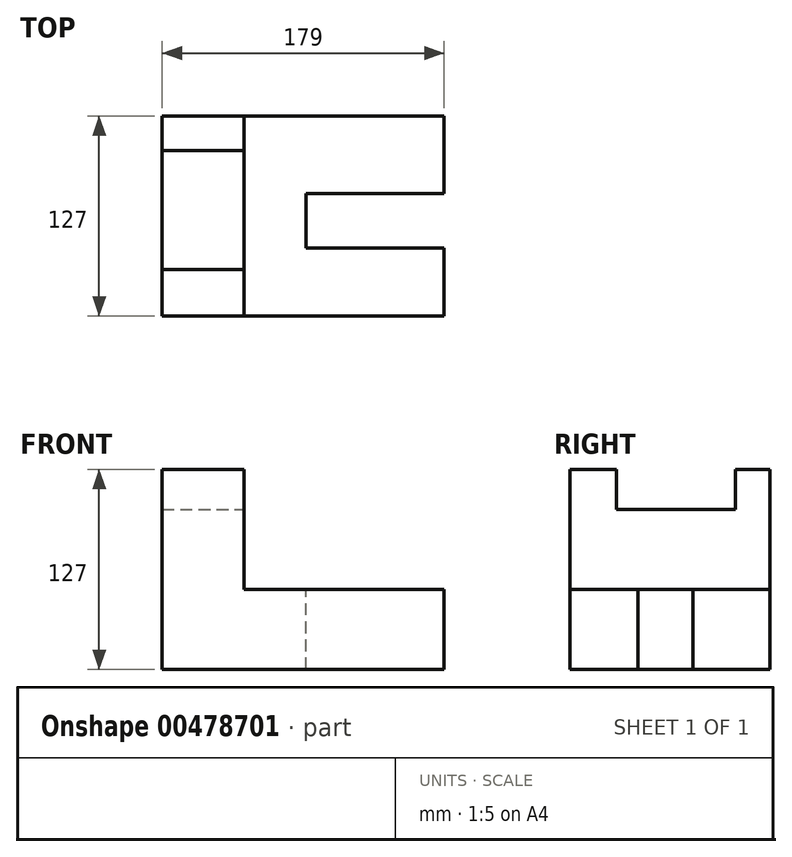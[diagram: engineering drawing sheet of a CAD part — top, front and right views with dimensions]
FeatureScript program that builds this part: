
annotation { "Feature Type Name" : "Feature", "Feature Type Description" : "" }
export const myFeature = defineFeature(function(context is Context, id is Id, definition is map)
    precondition{}
    {
        {
            var Q0;
            Q0=qCreatedBy(makeId("Front.planeOp"),FACE);
            var sketch = newSketch(context, id + "F0", { "sketchPlane" : qUnion([Q0])});
            skLineSegment(sketch, "E0", {"start": v(-127, 76.2) * mm, "end": v(-127, -50.8) * mm});
            skLineSegment(sketch, "E1", {"start": v(-127, -50.8) * mm, "end": v(52, -50.8) * mm});
            skLineSegment(sketch, "E2", {"start": v(52, -50.8) * mm, "end": v(52, 0) * mm});
            skLineSegment(sketch, "E3", {"start": v(52, 0) * mm, "end": v(-75, 0) * mm});
            skLineSegment(sketch, "E4", {"start": v(-75, 0) * mm, "end": v(-75, 76.2) * mm});
            skLineSegment(sketch, "E5", {"start": v(-75, 76.2) * mm, "end": v(-127, 76.2) * mm});
            skSolve(sketch);
        }
        {
            var Q0;
            Q0 = qSketchRegion(id + "F0", true);
            extrude(context, id + "F1", {"entities" : qUnion([Q0]), "depth" : 127 * mm});
        }
        {
            var Q0;
            Q0=makeQuery(id+"F1.opExtrude","SWEPT_FACE",FACE,{"disambiguationData":[OSD([sQuery(id+"F0.wireOp",EDGE,"E5")])]});
            var sketch = newSketch(context, id + "F2", { "sketchPlane" : qUnion([Q0])});
            skLineSegment(sketch, "E6", {"start": v(-127, -97.5) * mm, "end": v(-75, -97.5) * mm});
            skLineSegment(sketch, "E7", {"start": v(-127, -22) * mm, "end": v(-75, -22) * mm});
            skSolve(sketch);
        }
        {
            var Q0;
            {var subQ0=sQuery(id+"F2.wireOp",EDGE,"E6");Q0=makeQuery(id+"F2.imprint","IMPRINT",FACE,{"disambiguationData":[TD([[makeQuery(id+"F2.imprint","IMPRINT",EDGE,{"derivedFrom":subQ0}),1.0]])]});}
            extrude(context, id + "F3", {"entities" : qUnion([Q0]), "operationType" : NewBodyOperationType.REMOVE, "oppositeDirection" : true, "depth" : 25.4 * mm});
        }
        {
            var Q0;
            Q0=makeQuery(id+"F1.opExtrude","SWEPT_FACE",FACE,{"disambiguationData":[OSD([sQuery(id+"F0.wireOp",EDGE,"E3")])]});
            var sketch = newSketch(context, id + "F4", { "sketchPlane" : qUnion([Q0])});
            skLineSegment(sketch, "E8", {"start": v(52, -83.78) * mm, "end": v(-35.83, -83.78) * mm});
            skLineSegment(sketch, "E9", {"start": v(-35.83, -83.78) * mm, "end": v(-35.83, -49.1) * mm});
            skLineSegment(sketch, "E10", {"start": v(-35.83, -49.1) * mm, "end": v(52, -49.1) * mm});
            skPoint(sketch, "E10.endSnap0", {"position": v(52, -63.5) * mm});
            skSolve(sketch);
        }
        {
            var Q0;
            Q0 = qSketchRegion(id + "F4", true);
            var Q1;
            {var subQ0=sQuery(id+"F4.wireOp",EDGE,"E8");Q1=makeQuery(id+"F4.imprint","IMPRINT",FACE,{"disambiguationData":[TD([[makeQuery(id+"F4.imprint","IMPRINT",EDGE,{"derivedFrom":subQ0}),-1.0]])]});}
            extrude(context, id + "F5", {"entities" : qUnion([Q0, Q1]), "operationType" : NewBodyOperationType.REMOVE, "oppositeDirection" : true, "depth" : 77.47 * mm});
        }
    });
